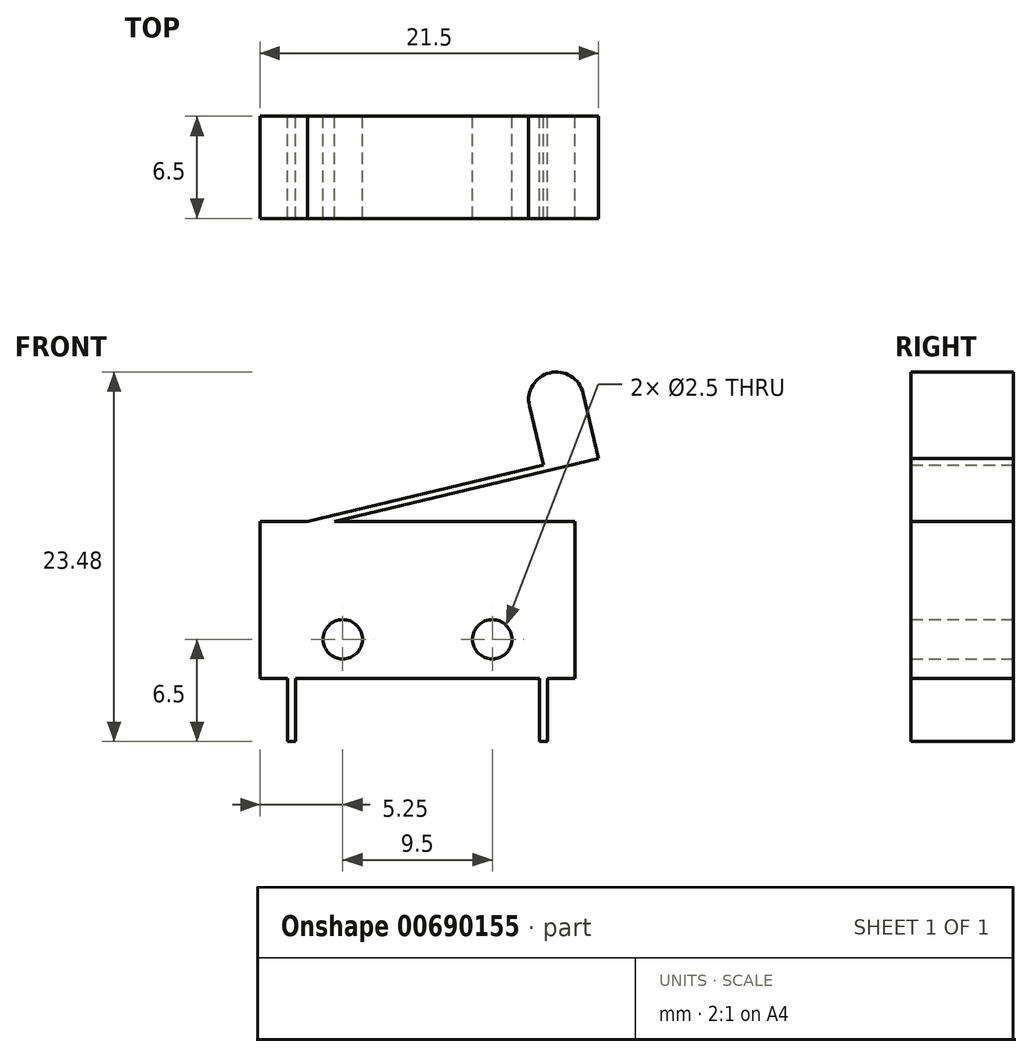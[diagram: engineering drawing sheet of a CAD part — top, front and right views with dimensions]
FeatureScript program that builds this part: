
annotation { "Feature Type Name" : "Feature", "Feature Type Description" : "" }
export const myFeature = defineFeature(function(context is Context, id is Id, definition is map)
    precondition{}
    {
        {
            var Q0;
            Q0=qCreatedBy(makeId("Front.planeOp"),FACE);
            var sketch = newSketch(context, id + "F0", { "sketchPlane" : qUnion([Q0])});
            skLineSegment(sketch, "E0.bottom", {"start": v(-10, 10) * mm, "end": v(10, 10) * mm});
            skLineSegment(sketch, "E0.top", {"start": v(-10, 0) * mm, "end": v(10, 0) * mm});
            skLineSegment(sketch, "E0.left", {"start": v(-10, 10) * mm, "end": v(-10, 0) * mm});
            skLineSegment(sketch, "E0.right", {"start": v(10, 10) * mm, "end": v(10, 0) * mm});
            skLineSegment(sketch, "E1", {"start": v(-5.28, 10) * mm, "end": v(11.5, 14) * mm});
            skLineSegment(sketch, "E2", {"start": v(11.5, 14) * mm, "end": v(10.51, 18.13) * mm});
            skLineSegment(sketch, "E3", {"start": v(10.51, 18.13) * mm, "end": v(7.1, 17.32) * mm, "construction": true});
            skLineSegment(sketch, "E4", {"start": v(7.1, 17.32) * mm, "end": v(8, 13.58) * mm});
            skLineSegment(sketch, "E5", {"start": v(8, 13.58) * mm, "end": v(-7, 10) * mm});
            skLineSegment(sketch, "E6", {"start": v(8.25, 0) * mm, "end": v(8.25, -4) * mm});
            skLineSegment(sketch, "E7", {"start": v(8.25, -4) * mm, "end": v(7.75, -4) * mm});
            skLineSegment(sketch, "E8", {"start": v(7.75, -4) * mm, "end": v(7.75, 0) * mm});
            skLineSegment(sketch, "E9.MirrorCS", {"start": v(-8.25, -4) * mm, "end": v(-7.75, -4) * mm});
            skLineSegment(sketch, "E10.MirrorCS", {"start": v(-7.75, -4) * mm, "end": v(-7.75, 0) * mm});
            skLineSegment(sketch, "E11.MirrorCS", {"start": v(-8.25, 0) * mm, "end": v(-8.25, -4) * mm});
            skCircle(sketch, "E12", {"center": v(4.75, 2.5) * mm, "radius": 1.25 * mm});
            skCircle(sketch, "E13.MirrorC", {"center": v(-4.75, 2.5) * mm, "radius": 1.25 * mm});
            skArc(sketch, "E14", {"start": v(10.51, 18.13) * mm, "mid": v(8.4, 19.43) * mm, "end": v(7.1, 17.32) * mm});
            skSolve(sketch);
        }
        {
            var Q0;
            Q0 = qSketchRegion(id + "F0", true);
            extrude(context, id + "F1", {"entities" : qUnion([Q0]), "endBound" : BoundingType.SYMMETRIC, "depth" : 6.5 * mm, "offsetDistance" : 25 * mm});
        }
    });
